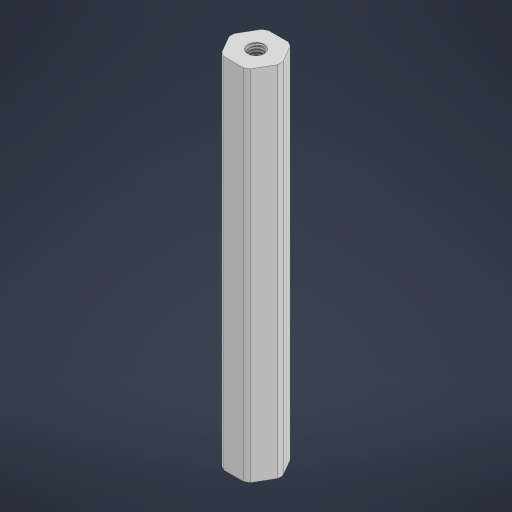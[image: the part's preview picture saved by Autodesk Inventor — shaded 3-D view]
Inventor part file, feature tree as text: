
AUTODESK INVENTOR PART (.ipt)
format: ipt  version: 2023 (Build 270158000, 158)  size: 1,021,952 bytes
history: native  units: in
note: dims shown in document units (in); Inventor stores cm internally (conversion verified against a paired STEP export)
features: mirror x1
ambient origin geometry x8: Origin, YZ Plane, XZ Plane, XY Plane, X Axis, Y Axis, Z Axis, Center Point
bodies: Solid1 (feature_tree)
feature tree (1):
  mirror  "Mirror2"
